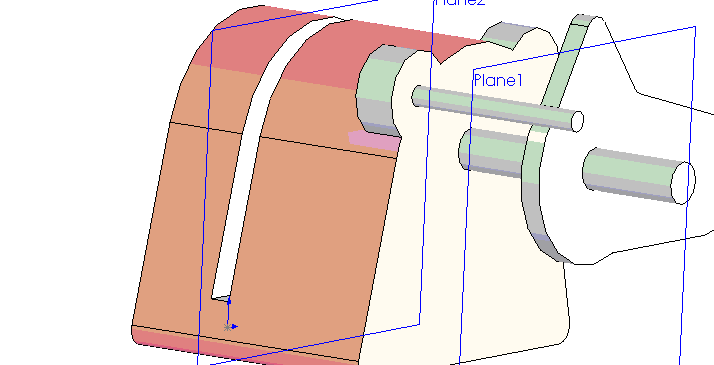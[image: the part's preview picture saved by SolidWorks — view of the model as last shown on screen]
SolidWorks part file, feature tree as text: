
SOLIDWORKS PART (.sldprt)
format: sldprt  version: not decoded by parser v0  size: 246,272 bytes
history: native  units: mm
features: sketch x6, extrude x5, plane x2, cut_extrude x1 (+11 scaffold rows collapsed)
feature tree (25):
  scaffold x11  (default folders/planes/origin — collapsed)
  sketch  "Sketch1"  dims[c1.D4=2.54mm c1.D1=55.372mm c1.D2=38.862mm c1.D3=32.512mm c2.D4=~38.492483mm]
  extrude  "Extrude1"  Depth=40.64mm
  sketch  "Sketch2"  dims[D1=13.716mm D2=41.275mm]
  extrude  "Extrude2"  Depth=6.35mm
  sketch  "Sketch3"  dims[D1=3.175mm D2=~0.47438mm]
  extrude  "Extrude3"  Depth=28.575mm
  sketch  "Sketch4"  dims[D1=6.35mm]
  extrude  "Extrude4"  Depth=38.1mm
  plane  "Plane1"  Offset=19.05mm
  sketch  "Sketch5"  dims[D1=8.89mm D2=28.575mm D3=2.54mm]
  extrude  "Extrude5"  Depth=3.175mm
  plane  "Plane2"  Offset=12.954mm
  sketch  "Sketch6"
  cut_extrude  "Cut-Extrude1"  Depth=3.175mm
decode coverage: 11 of 12 modeling features carry decoded parameters
note: ~ marks probable driven/reference dimensions
note: suppression state not decoded; provenance and decode notes live in map.json
